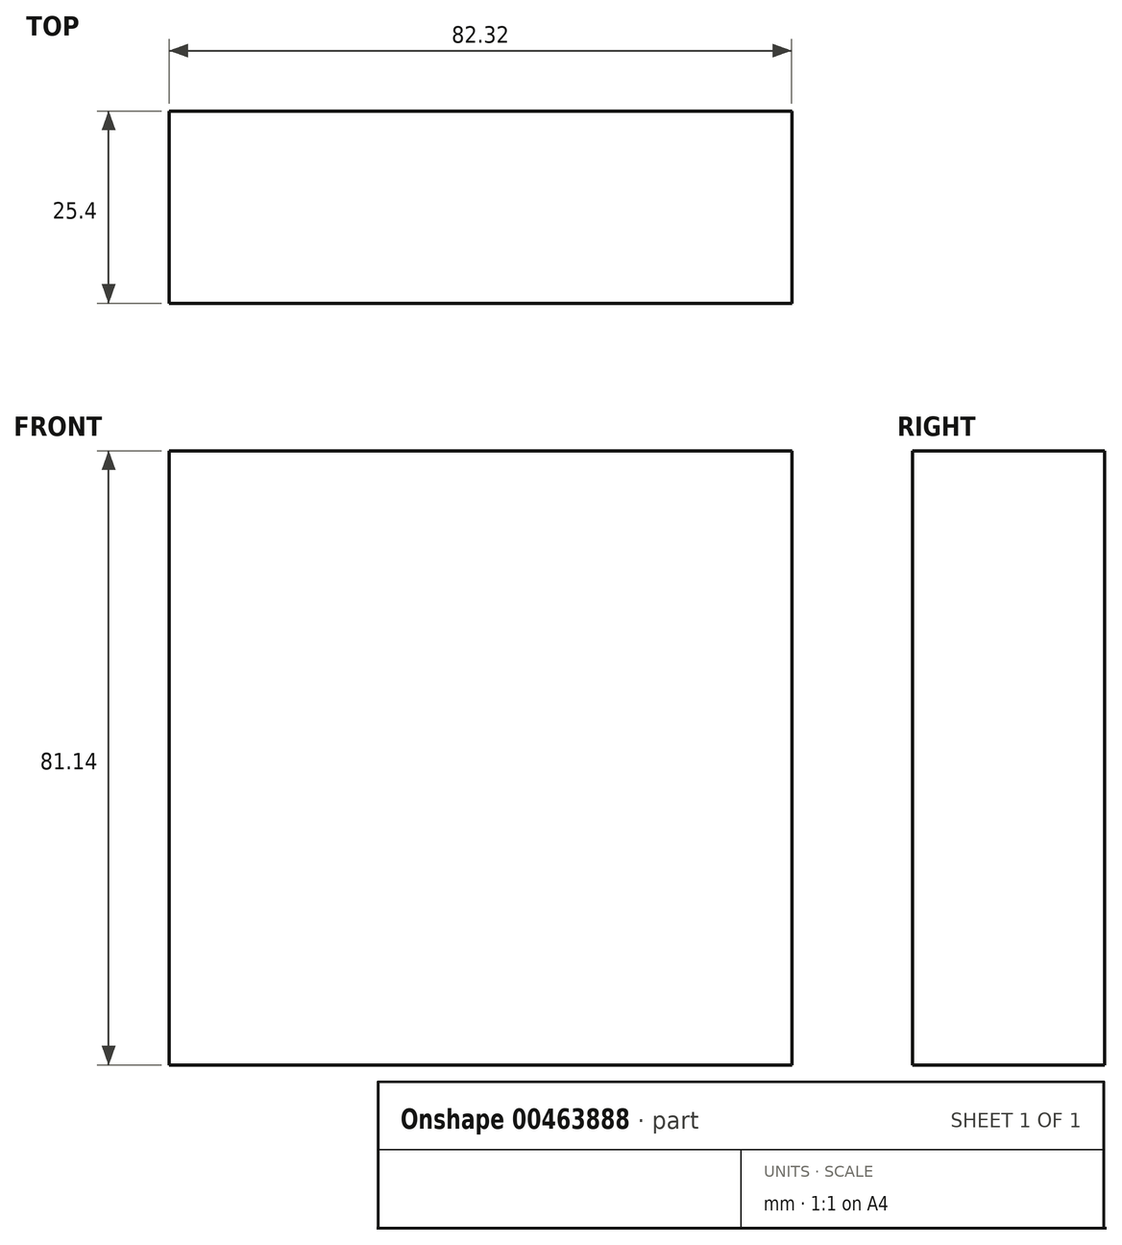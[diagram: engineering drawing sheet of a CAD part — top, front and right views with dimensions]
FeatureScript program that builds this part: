
annotation { "Feature Type Name" : "Feature", "Feature Type Description" : "" }
export const myFeature = defineFeature(function(context is Context, id is Id, definition is map)
    precondition{}
    {
        {
            var Q0;
            Q0=qCreatedBy(makeId("Front.planeOp"),FACE);
            var sketch = newSketch(context, id + "F0", { "sketchPlane" : qUnion([Q0])});
            skLineSegment(sketch, "E0.bottom", {"start": v(-30.66, 41.84) * mm, "end": v(51.66, 41.84) * mm});
            skLineSegment(sketch, "E0.top", {"start": v(-30.66, -39.3) * mm, "end": v(51.66, -39.3) * mm});
            skLineSegment(sketch, "E0.left", {"start": v(-30.66, 41.84) * mm, "end": v(-30.66, -39.3) * mm});
            skLineSegment(sketch, "E0.right", {"start": v(51.66, 41.84) * mm, "end": v(51.66, -39.3) * mm});
            skSolve(sketch);
        }
        {
            var Q0;
            Q0=sQuery(id+"F0.wireOp",EDGE,"E0.right");
            var Q1;
            Q1=sQuery(id+"F0.wireOp",EDGE,"E0.top");
            var Q2;
            Q2=sQuery(id+"F0.wireOp",EDGE,"E0.left");
            var Q3;
            Q3=sQuery(id+"F0.wireOp",EDGE,"E0.bottom");
            extrude(context, id + "F1", {"bodyType" : ToolBodyType.SURFACE, "surfaceEntities" : qUnion([Q0, Q1, Q2, Q3]), "depth" : 25.4 * mm});
        }
    });
